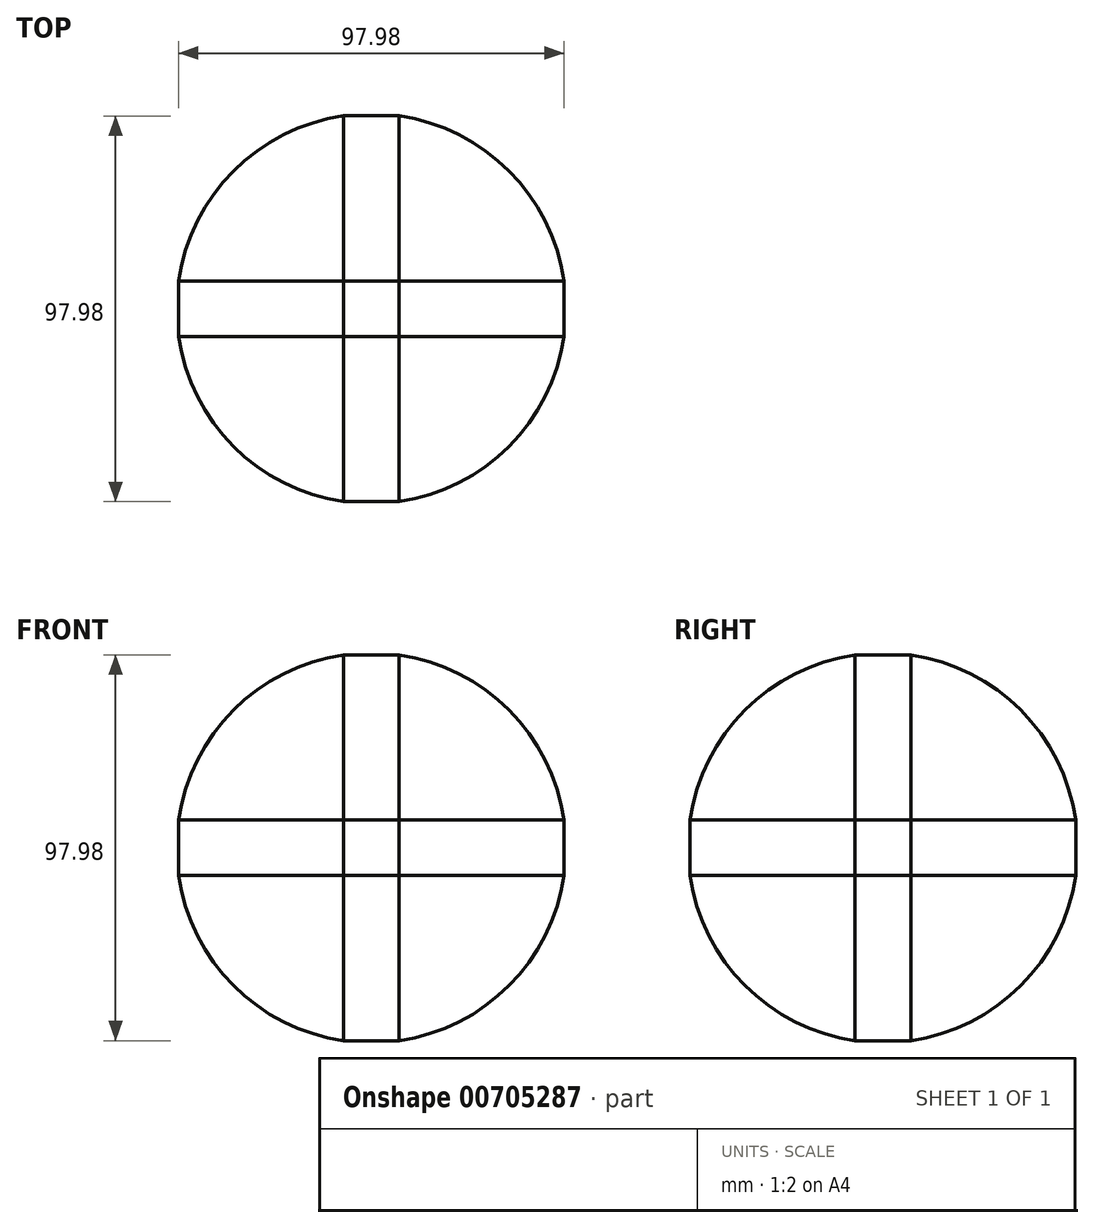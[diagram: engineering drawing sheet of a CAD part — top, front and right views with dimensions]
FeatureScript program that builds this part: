
annotation { "Feature Type Name" : "Feature", "Feature Type Description" : "" }
export const myFeature = defineFeature(function(context is Context, id is Id, definition is map)
    precondition{}
    {
        {
            var Q0;
            Q0=qCreatedBy(makeId("Top.planeOp"),FACE);
            var sketch = newSketch(context, id + "F0", { "sketchPlane" : qUnion([Q0])});
            skCircle(sketch, "E0", {"center": v(0, 0) * mm, "radius": 50 * mm});
            skLineSegment(sketch, "E1", {"start": v(0, 0) * mm, "end": v(69.26, 0) * mm, "construction": true});
            skLineSegment(sketch, "E2", {"start": v(0, 0) * mm, "end": v(-59.91, 0) * mm});
            skLineSegment(sketch, "E3", {"start": v(-59.91, 0) * mm, "end": v(73.8, 0) * mm});
            skSolve(sketch);
        }
        {
            var Q0;
            {var subQ0=sQuery(id+"F0.wireOp",EDGE,"E2");var subQ1=sQuery(id+"F0.wireOp",EDGE,"E0");var subQ2=makeQuery(id+"F0.imprint","INTERSECT",VERTEX,{"derivedFrom":[subQ1,subQ0]});Q0=makeQuery(id+"F0.imprint","IMPRINT",FACE,{"disambiguationData":[TD([[makeQuery(id+"F0.imprint","IMPRINT",EDGE,{"disambiguationData":[TD([[subQ2,1.0]])],"derivedFrom":subQ1}),1.0]])]});}
            var Q1;
            Q1=sQuery(id+"F0.wireOp",EDGE,"E3");
            revolve(context, id + "F1", {"surfaceOperationType" : NewSurfaceOperationType.NEW, "entities" : qUnion([Q0]), "axis" : qUnion([Q1]), "revolveType" : RevolveType.FULL});
        }
        {
            var Q0;
            Q0=qCreatedBy(makeId("Top.planeOp"),FACE);
            cPlane(context, id + "F2", {"entities" : qUnion([Q0]), "cplaneType" : CPlaneType.OFFSET, "offset" : 60 * mm, "width" : 150 * mm, "height" : 150 * mm});
        }
        {
            var Q0;
            Q0=qCreatedBy(id+"F2.planeOp",FACE);
            var sketch = newSketch(context, id + "F3", { "sketchPlane" : qUnion([Q0])});
            skCircle(sketch, "E4", {"center": v(0, 0) * mm, "radius": 49.5 * mm});
            skCircle(sketch, "E5", {"center": v(0, 0) * mm, "radius": 131.03 * mm});
            skSolve(sketch);
        }
        {
            var Q0;
            Q0=makeQuery(id+"F3.imprint","IMPRINT",FACE,{"disambiguationData":[TD([[makeQuery(id+"F3.imprint","IMPRINT",EDGE,{"derivedFrom":sQuery(id+"F3.wireOp",EDGE,"E4")}),-1.0]])]});
            extrude(context, id + "F4", {"entities" : qUnion([Q0]), "operationType" : NewBodyOperationType.REMOVE, "endBound" : BoundingType.THROUGH_ALL, "oppositeDirection" : true, "depth" : 25 * mm, "offsetDistance" : 25 * mm});
        }
        {
            var Q0;
            Q0=qCreatedBy(makeId("Front.planeOp"),FACE);
            cPlane(context, id + "F5", {"entities" : qUnion([Q0]), "cplaneType" : CPlaneType.OFFSET, "offset" : 60 * mm, "width" : 150 * mm, "height" : 150 * mm});
        }
        {
            var Q0;
            Q0=qCreatedBy(makeId("Right.planeOp"),FACE);
            cPlane(context, id + "F6", {"entities" : qUnion([Q0]), "cplaneType" : CPlaneType.OFFSET, "offset" : 60 * mm, "width" : 150 * mm, "height" : 150 * mm});
        }
        {
            var Q0;
            Q0=qCreatedBy(id+"F5.planeOp",FACE);
            var sketch = newSketch(context, id + "F7", { "sketchPlane" : qUnion([Q0])});
            skCircle(sketch, "E6", {"center": v(0, 0) * mm, "radius": 49.5 * mm});
            skCircle(sketch, "E7", {"center": v(0, 0) * mm, "radius": 68.91 * mm});
            skSolve(sketch);
        }
        {
            var Q0;
            Q0=makeQuery(id+"F7.imprint","IMPRINT",FACE,{"disambiguationData":[TD([[makeQuery(id+"F7.imprint","IMPRINT",EDGE,{"derivedFrom":sQuery(id+"F7.wireOp",EDGE,"E6")}),-1.0]])]});
            extrude(context, id + "F8", {"entities" : qUnion([Q0]), "operationType" : NewBodyOperationType.REMOVE, "endBound" : BoundingType.THROUGH_ALL, "oppositeDirection" : true, "depth" : 25 * mm, "offsetDistance" : 25 * mm});
        }
        {
            var Q0;
            Q0=qCreatedBy(id+"F6.planeOp",FACE);
            var sketch = newSketch(context, id + "F9", { "sketchPlane" : qUnion([Q0])});
            skCircle(sketch, "E8", {"center": v(0, 0) * mm, "radius": 49.5 * mm});
            skCircle(sketch, "E9", {"center": v(0, 0) * mm, "radius": 79.7 * mm});
            skSolve(sketch);
        }
        {
            var Q0;
            Q0=makeQuery(id+"F9.imprint","IMPRINT",FACE,{"disambiguationData":[TD([[makeQuery(id+"F9.imprint","IMPRINT",EDGE,{"derivedFrom":sQuery(id+"F9.wireOp",EDGE,"E8")}),-1.0]])]});
            extrude(context, id + "F10", {"entities" : qUnion([Q0]), "operationType" : NewBodyOperationType.REMOVE, "endBound" : BoundingType.THROUGH_ALL, "oppositeDirection" : true, "depth" : 25 * mm, "offsetDistance" : 25 * mm});
        }
        {
            var Q0;
            Q0=qCreatedBy(makeId("Top.planeOp"),FACE);
            var Q1;
            Q1=makeQuery(id+"F10.boolean.opBoolean","INTERSECT",VERTEX,{"disambiguationData":[OD(1.0)],"derivedFrom":[makeQuery(id+"F8.boolean.opBoolean","SPLIT",FACE,{"disambiguationData":[OD(0.0)],"derivedFrom":makeQuery(id+"F4.boolean.opBoolean","SPLIT",FACE,{"disambiguationData":[OD(1.0)],"derivedFrom":makeQuery(id+"F1.opRevolve","SWEPT_FACE",FACE,{"disambiguationData":[OSD([sQuery(id+"F0.wireOp",EDGE,"E0")])]})})}),makeQuery(id+"F8.boolean.opBoolean","COPY",FACE,{"disambiguationData":[OD(1.0)],"derivedFrom":makeQuery(id+"F8.opExtrude","SWEPT_FACE",FACE,{"disambiguationData":[OSD([sQuery(id+"F7.wireOp",EDGE,"E6")])]})}),makeQuery(id+"F10.opExtrude","SWEPT_FACE",FACE,{"disambiguationData":[OSD([sQuery(id+"F9.wireOp",EDGE,"E8")])]})]});
            cPlane(context, id + "F11", {"entities" : qUnion([Q0, Q1]), "cplaneType" : CPlaneType.PLANE_POINT, "offset" : 25 * mm, "width" : 150 * mm, "height" : 150 * mm});
        }
        {
            var Q0;
            Q0=qCreatedBy(id+"F11.planeOp",FACE);
            var sketch = newSketch(context, id + "F12", { "sketchPlane" : qUnion([Q0])});
            skLineSegment(sketch, "E10.bottom", {"start": v(-7.05, -7.05) * mm, "end": v(7.05, -7.05) * mm});
            skLineSegment(sketch, "E10.top", {"start": v(-7.05, 7.05) * mm, "end": v(7.05, 7.05) * mm});
            skLineSegment(sketch, "E10.left", {"start": v(-7.05, -7.05) * mm, "end": v(-7.05, 7.05) * mm});
            skLineSegment(sketch, "E10.right", {"start": v(7.05, -7.05) * mm, "end": v(7.05, 7.05) * mm});
            skSolve(sketch);
        }
        {
            var Q0;
            Q0=makeQuery(id+"F12.imprint","IMPRINT",FACE,{"disambiguationData":[TD([[makeQuery(id+"F12.imprint","IMPRINT",EDGE,{"derivedFrom":sQuery(id+"F12.wireOp",EDGE,"E10.bottom")}),1.0]])]});
            extrude(context, id + "F13", {"entities" : qUnion([Q0]), "operationType" : NewBodyOperationType.REMOVE, "endBound" : BoundingType.THROUGH_ALL, "depth" : 25 * mm, "offsetDistance" : 25 * mm});
        }
        {
            var Q0;
            Q0=qCreatedBy(makeId("Front.planeOp"),FACE);
            var Q1;
            Q1=makeQuery(id+"F10.boolean.opBoolean","INTERSECT",VERTEX,{"disambiguationData":[OD(1.0)],"derivedFrom":[makeQuery(id+"F8.boolean.opBoolean","SPLIT",FACE,{"disambiguationData":[OD(0.0)],"derivedFrom":makeQuery(id+"F4.boolean.opBoolean","COPY",FACE,{"derivedFrom":makeQuery(id+"F4.opExtrude","SWEPT_FACE",FACE,{"disambiguationData":[OSD([sQuery(id+"F3.wireOp",EDGE,"E4")])]})})}),makeQuery(id+"F8.boolean.opBoolean","SPLIT",FACE,{"disambiguationData":[OD(0.0)],"derivedFrom":makeQuery(id+"F4.boolean.opBoolean","SPLIT",FACE,{"disambiguationData":[OD(1.0)],"derivedFrom":makeQuery(id+"F1.opRevolve","SWEPT_FACE",FACE,{"disambiguationData":[OSD([sQuery(id+"F0.wireOp",EDGE,"E0")])]})})}),makeQuery(id+"F10.opExtrude","SWEPT_FACE",FACE,{"disambiguationData":[OSD([sQuery(id+"F9.wireOp",EDGE,"E8")])]})]});
            cPlane(context, id + "F14", {"entities" : qUnion([Q0, Q1]), "cplaneType" : CPlaneType.PLANE_POINT, "offset" : 25 * mm, "width" : 150 * mm, "height" : 150 * mm});
        }
        {
            var Q0;
            Q0=qCreatedBy(id+"F14.planeOp",FACE);
            var sketch = newSketch(context, id + "F15", { "sketchPlane" : qUnion([Q0])});
            skLineSegment(sketch, "E11.bottom", {"start": v(-7.05, -7.05) * mm, "end": v(7.05, -7.05) * mm});
            skLineSegment(sketch, "E11.top", {"start": v(-7.05, 7.05) * mm, "end": v(7.05, 7.05) * mm});
            skLineSegment(sketch, "E11.left", {"start": v(-7.05, -7.05) * mm, "end": v(-7.05, 7.05) * mm});
            skLineSegment(sketch, "E11.right", {"start": v(7.05, -7.05) * mm, "end": v(7.05, 7.05) * mm});
            skSolve(sketch);
        }
        {
            var Q0;
            Q0 = qSketchRegion(id + "F15", true);
            extrude(context, id + "F16", {"entities" : qUnion([Q0]), "operationType" : NewBodyOperationType.REMOVE, "endBound" : BoundingType.THROUGH_ALL, "depth" : 25 * mm, "offsetDistance" : 25 * mm});
        }
        {
            var Q0;
            Q0=qCreatedBy(makeId("Top.planeOp"),FACE);
            var sketch = newSketch(context, id + "F17", { "sketchPlane" : qUnion([Q0])});
            skLineSegment(sketch, "E12.bottom", {"start": v(-59.01, 7.05) * mm, "end": v(-49, 7.05) * mm});
            skLineSegment(sketch, "E12.top", {"start": v(-59.01, -7.05) * mm, "end": v(-49, -7.05) * mm});
            skLineSegment(sketch, "E12.left", {"start": v(-59.01, 7.05) * mm, "end": v(-59.01, -7.05) * mm});
            skLineSegment(sketch, "E12.right", {"start": v(-49, 7.05) * mm, "end": v(-49, -7.05) * mm});
            skLineSegment(sketch, "E13.bottom", {"start": v(-7.05, 59.02) * mm, "end": v(7.05, 59.02) * mm});
            skLineSegment(sketch, "E13.top", {"start": v(-7.05, 49) * mm, "end": v(7.05, 49) * mm});
            skLineSegment(sketch, "E13.left", {"start": v(-7.05, 59.02) * mm, "end": v(-7.05, 49) * mm});
            skLineSegment(sketch, "E13.right", {"start": v(7.05, 59.02) * mm, "end": v(7.05, 49) * mm});
            skLineSegment(sketch, "E14.bottom", {"start": v(63.53, 7.05) * mm, "end": v(49, 7.05) * mm});
            skLineSegment(sketch, "E14.top", {"start": v(63.53, -7.05) * mm, "end": v(49, -7.05) * mm});
            skLineSegment(sketch, "E14.left", {"start": v(63.53, 7.05) * mm, "end": v(63.53, -7.05) * mm});
            skLineSegment(sketch, "E14.right", {"start": v(49, 7.05) * mm, "end": v(49, -7.05) * mm});
            skLineSegment(sketch, "E15.bottom", {"start": v(-7.05, -64.03) * mm, "end": v(7.05, -64.03) * mm});
            skLineSegment(sketch, "E15.top", {"start": v(-7.05, -49) * mm, "end": v(7.05, -49) * mm});
            skLineSegment(sketch, "E15.left", {"start": v(-7.05, -64.03) * mm, "end": v(-7.05, -49) * mm});
            skLineSegment(sketch, "E15.right", {"start": v(7.05, -64.03) * mm, "end": v(7.05, -49) * mm});
            skSolve(sketch);
        }
        {
            var Q0;
            Q0 = qSketchRegion(id + "F17", true);
            extrude(context, id + "F18", {"entities" : qUnion([Q0]), "operationType" : NewBodyOperationType.REMOVE, "endBound" : BoundingType.THROUGH_ALL, "oppositeDirection" : true, "depth" : 25 * mm, "offsetDistance" : 25 * mm, "hasSecondDirection" : true, "secondDirectionBound" : SecondDirectionBoundingType.THROUGH_ALL, "secondDirectionOppositeDirection" : false, "secondDirectionDepth" : 25 * mm});
        }
        {
            var Q0;
            Q0=qCreatedBy(makeId("Front.planeOp"),FACE);
            var sketch = newSketch(context, id + "F19", { "sketchPlane" : qUnion([Q0])});
            skLineSegment(sketch, "E16.bottom", {"start": v(-7.05, -49) * mm, "end": v(7.05, -49) * mm});
            skLineSegment(sketch, "E16.top", {"start": v(-7.05, -56.99) * mm, "end": v(7.05, -56.99) * mm});
            skLineSegment(sketch, "E16.left", {"start": v(-7.05, -49) * mm, "end": v(-7.05, -56.99) * mm});
            skLineSegment(sketch, "E16.right", {"start": v(7.05, -49) * mm, "end": v(7.05, -56.99) * mm});
            skSolve(sketch);
        }
        {
            var Q0;
            Q0 = qSketchRegion(id + "F19", true);
            extrude(context, id + "F20", {"entities" : qUnion([Q0]), "operationType" : NewBodyOperationType.REMOVE, "endBound" : BoundingType.THROUGH_ALL, "oppositeDirection" : true, "depth" : 25 * mm, "offsetDistance" : 25 * mm, "hasSecondDirection" : true, "secondDirectionOppositeDirection" : false, "secondDirectionDepth" : 25 * mm});
        }
    });
